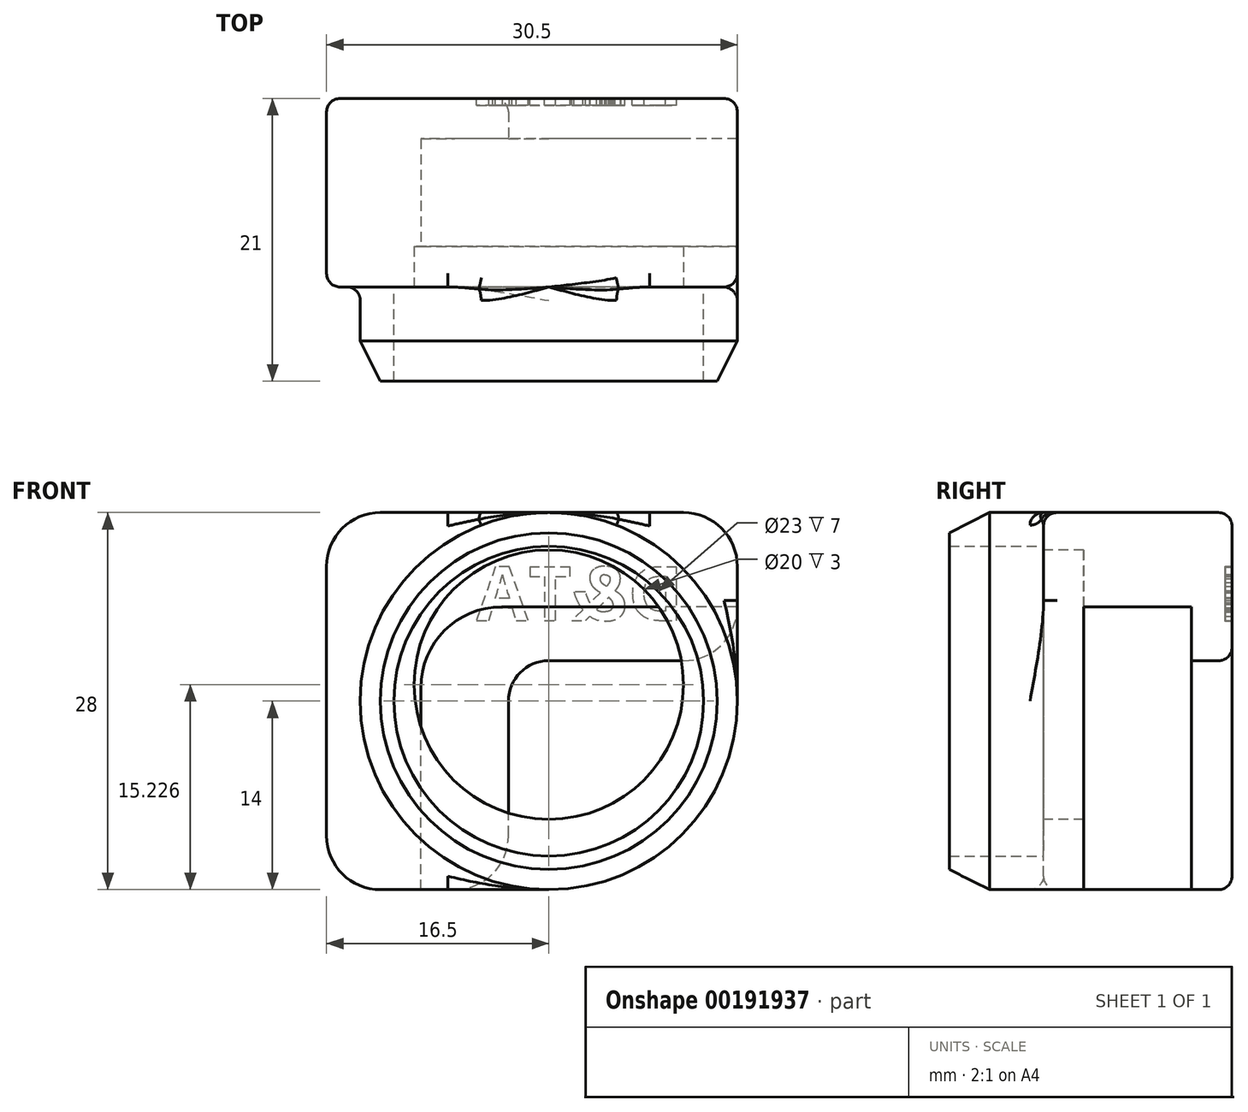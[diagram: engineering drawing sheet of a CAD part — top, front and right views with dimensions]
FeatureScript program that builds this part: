
annotation { "Feature Type Name" : "Feature", "Feature Type Description" : "" }
export const myFeature = defineFeature(function(context is Context, id is Id, definition is map)
    precondition{}
    {
        {
            var Q0;
            Q0=qCreatedBy(makeId("Front.planeOp"),FACE);
            var sketch = newSketch(context, id + "F0", { "sketchPlane" : qUnion([Q0])});
            skCircle(sketch, "E0", {"center": v(0, 0) * mm, "radius": 14 * mm});
            skCircle(sketch, "E1", {"center": v(0, 0) * mm, "radius": 11.5 * mm});
            skSolve(sketch);
        }
        {
            var Q0;
            Q0=makeQuery(id+"F0.imprint","IMPRINT",FACE,{"disambiguationData":[TD([[makeQuery(id+"F0.imprint","IMPRINT",EDGE,{"derivedFrom":sQuery(id+"F0.wireOp",EDGE,"E0")}),1.0]])]});
            extrude(context, id + "F1", {"entities" : qUnion([Q0]), "depth" : 10 * mm});
        }
        {
            var Q0;
            Q0=qCreatedBy(makeId("Front.planeOp"),FACE);
            var sketch = newSketch(context, id + "F2", { "sketchPlane" : qUnion([Q0])});
            skLineSegment(sketch, "E2", {"start": v(-9.5, -14) * mm, "end": v(-16.5, -14) * mm});
            skLineSegment(sketch, "E3", {"start": v(-16.5, -14) * mm, "end": v(-16.5, 14) * mm});
            skLineSegment(sketch, "E4", {"start": v(-16.5, 14) * mm, "end": v(14, 14) * mm});
            skLineSegment(sketch, "E5", {"start": v(14, 14) * mm, "end": v(14, 7) * mm});
            skLineSegment(sketch, "E6", {"start": v(14, 7) * mm, "end": v(-3.5, 7) * mm});
            skLineSegment(sketch, "E7", {"start": v(-9.5, -14) * mm, "end": v(-9.5, 1) * mm});
            skArc(sketch, "E8", {"start": v(-3.5, 7) * mm, "mid": v(-7.74, 5.24) * mm, "end": v(-9.5, 1) * mm});
            skSolve(sketch);
        }
        {
            var Q0;
            Q0=makeQuery(id+"F2.imprint","IMPRINT",FACE,{"disambiguationData":[TD([[makeQuery(id+"F2.imprint","IMPRINT",EDGE,{"derivedFrom":sQuery(id+"F2.wireOp",EDGE,"E2")}),-1.0]])]});
            extrude(context, id + "F3", {"entities" : qUnion([Q0]), "operationType" : NewBodyOperationType.ADD, "oppositeDirection" : true, "depth" : 8 * mm});
        }
        {
            var Q0;
            Q0=makeQuery(id+"F1.opExtrude","CAP_FACE",FACE,{"disambiguationData":[OSD([sQuery(id+"F0.wireOp",EDGE,"E0"),sQuery(id+"F0.wireOp",EDGE,"E1")])],"isStart":true});
            var sketch = newSketch(context, id + "F4", { "sketchPlane" : qUnion([Q0])});
            skArc(sketch, "E9", {"start": v(-14, 0) * mm, "mid": v(-9.9, -9.9) * mm, "end": v(0, -14) * mm});
            skLineSegment(sketch, "E10", {"start": v(16.5, 14) * mm, "end": v(-14, 14) * mm});
            skLineSegment(sketch, "E11", {"start": v(-14, 14) * mm, "end": v(-14, 0) * mm});
            skLineSegment(sketch, "E12", {"start": v(16.5, 14) * mm, "end": v(16.5, -14) * mm});
            skLineSegment(sketch, "E13", {"start": v(16.5, -14) * mm, "end": v(0, -14) * mm});
            skSolve(sketch);
        }
        {
            var Q0;
            Q0=makeQuery(id+"F4.imprint","IMPRINT",FACE,{"disambiguationData":[TD([[makeQuery(id+"F4.imprint","IMPRINT",EDGE,{"derivedFrom":sQuery(id+"F4.wireOp",EDGE,"E10")}),1.0]])]});
            extrude(context, id + "F5", {"entities" : qUnion([Q0]), "operationType" : NewBodyOperationType.ADD, "oppositeDirection" : true, "depth" : 3 * mm});
        }
        {
            var Q0;
            Q0=makeQuery(id+"F3.opExtrude","CAP_FACE",FACE,{"disambiguationData":[OSD([sQuery(id+"F2.wireOp",EDGE,"E2"),sQuery(id+"F2.wireOp",EDGE,"E3"),sQuery(id+"F2.wireOp",EDGE,"E4"),sQuery(id+"F2.wireOp",EDGE,"E5"),sQuery(id+"F2.wireOp",EDGE,"E6"),sQuery(id+"F2.wireOp",EDGE,"E7"),sQuery(id+"F2.wireOp",EDGE,"E8")])],"isStart":false});
            var sketch = newSketch(context, id + "F6", { "sketchPlane" : qUnion([Q0])});
            skLineSegment(sketch, "E14", {"start": v(-14, 14) * mm, "end": v(16.5, 14) * mm});
            skLineSegment(sketch, "E15", {"start": v(16.5, 14) * mm, "end": v(16.5, -14) * mm});
            skLineSegment(sketch, "E16", {"start": v(16.5, -14) * mm, "end": v(3, -14) * mm});
            skLineSegment(sketch, "E17", {"start": v(3, -14) * mm, "end": v(3, 0) * mm});
            skLineSegment(sketch, "E18", {"start": v(-14, 14) * mm, "end": v(-14, 3) * mm});
            skLineSegment(sketch, "E19", {"start": v(-14, 3) * mm, "end": v(0, 3) * mm});
            skArc(sketch, "E20", {"start": v(3, 0) * mm, "mid": v(2.12, 2.12) * mm, "end": v(0, 3) * mm});
            skSolve(sketch);
        }
        {
            var Q0;
            {var subQ0=sQuery(id+"F0.wireOp",EDGE,"E0");Q0=makeQuery(id+"F5.boolean.opBoolean","INTERSECT",EDGE,{"disambiguationData":[OD(0.0)],"derivedFrom":[makeQuery(id+"F1.opExtrude","SWEPT_FACE",FACE,{"disambiguationData":[OSD([subQ0])]}),makeQuery(id+"F5.opExtrude","CAP_FACE",FACE,{"disambiguationData":[OSD([subQ0,sQuery(id+"F0.wireOp",EDGE,"E1"),sQuery(id+"F2.wireOp",EDGE,"E6"),sQuery(id+"F2.wireOp",EDGE,"E7"),sQuery(id+"F4.wireOp",EDGE,"E10"),sQuery(id+"F4.wireOp",EDGE,"E11"),sQuery(id+"F4.wireOp",EDGE,"E12"),sQuery(id+"F4.wireOp",EDGE,"E13")])],"isStart":false})]});}
            fillet(context, id + "F7", {"entities" : qUnion([Q0]), "radius" : 1 * mm, "tangentPropagation" : true, "allowEdgeOverflow" : false});
        }
        {
            var Q0;
            {var subQ3=sQuery(id+"F6.wireOp",EDGE,"E17");Q0=makeQuery(id+"F6.imprint","IMPRINT",FACE,{"disambiguationData":[TD([[makeQuery(id+"F6.imprint","IMPRINT",EDGE,{"derivedFrom":subQ3}),-1.0]])]});}
            var Q1;
            {var subQ4=sQuery(id+"F6.wireOp",EDGE,"E14");Q1=makeQuery(id+"F6.imprint","IMPRINT",FACE,{"disambiguationData":[TD([[makeQuery(id+"F6.imprint","IMPRINT",EDGE,{"derivedFrom":subQ4}),1.0]])]});}
            extrude(context, id + "F8", {"entities" : qUnion([Q0, Q1]), "operationType" : NewBodyOperationType.ADD, "depth" : 3 * mm});
        }
        {
            var Q0;
            Q0=makeQuery(id+"F8.boolean.opBoolean","MERGE",EDGE,{"derivedFrom":[makeQuery(id+"F5.boolean.opBoolean","MERGE",EDGE,{"derivedFrom":[makeQuery(id+"F3.opExtrude","SWEPT_EDGE",EDGE,{"disambiguationData":[OSD([sQuery(id+"F2.wireOp",EDGE,"E2"),sQuery(id+"F2.wireOp",EDGE,"E3")])]}),makeQuery(id+"F5.opExtrude","SWEPT_EDGE",EDGE,{"disambiguationData":[OSD([sQuery(id+"F4.wireOp",EDGE,"E12"),sQuery(id+"F4.wireOp",EDGE,"E13")])]})]}),makeQuery(id+"F8.opExtrude","SWEPT_EDGE",EDGE,{"disambiguationData":[OSD([sQuery(id+"F6.wireOp",EDGE,"E15"),sQuery(id+"F6.wireOp",EDGE,"E16")])]})]});
            var Q1;
            Q1=makeQuery(id+"F8.boolean.opBoolean","MERGE",EDGE,{"derivedFrom":[makeQuery(id+"F5.boolean.opBoolean","MERGE",EDGE,{"derivedFrom":[makeQuery(id+"F3.opExtrude","SWEPT_EDGE",EDGE,{"disambiguationData":[OSD([sQuery(id+"F2.wireOp",EDGE,"E4"),sQuery(id+"F2.wireOp",EDGE,"E5")])]}),makeQuery(id+"F5.opExtrude","SWEPT_EDGE",EDGE,{"disambiguationData":[OSD([sQuery(id+"F4.wireOp",EDGE,"E10"),sQuery(id+"F4.wireOp",EDGE,"E11")])]})]}),makeQuery(id+"F8.opExtrude","SWEPT_EDGE",EDGE,{"disambiguationData":[OSD([sQuery(id+"F6.wireOp",EDGE,"E14"),sQuery(id+"F6.wireOp",EDGE,"E18")])]})]});
            var Q2;
            Q2=makeQuery(id+"F8.opExtrude","SWEPT_EDGE",EDGE,{"disambiguationData":[OSD([sQuery(id+"F6.wireOp",EDGE,"E16"),sQuery(id+"F6.wireOp",EDGE,"E17")])]});
            var Q3;
            Q3=makeQuery(id+"F8.opExtrude","SWEPT_EDGE",EDGE,{"disambiguationData":[OSD([sQuery(id+"F6.wireOp",EDGE,"E18"),sQuery(id+"F6.wireOp",EDGE,"E19")])]});
            var Q4;
            Q4=makeQuery(id+"F8.boolean.opBoolean","MERGE",EDGE,{"derivedFrom":[makeQuery(id+"F5.boolean.opBoolean","MERGE",EDGE,{"derivedFrom":[makeQuery(id+"F3.opExtrude","SWEPT_EDGE",EDGE,{"disambiguationData":[OSD([sQuery(id+"F2.wireOp",EDGE,"E3"),sQuery(id+"F2.wireOp",EDGE,"E4")])]}),makeQuery(id+"F5.opExtrude","SWEPT_EDGE",EDGE,{"disambiguationData":[OSD([sQuery(id+"F4.wireOp",EDGE,"E10"),sQuery(id+"F4.wireOp",EDGE,"E12")])]})]}),makeQuery(id+"F8.opExtrude","SWEPT_EDGE",EDGE,{"disambiguationData":[OSD([sQuery(id+"F6.wireOp",EDGE,"E14"),sQuery(id+"F6.wireOp",EDGE,"E15")])]})]});
            fillet(context, id + "F9", {"entities" : qUnion([Q0, Q1, Q2, Q3, Q4]), "radius" : 4 * mm, "tangentPropagation" : true, "allowEdgeOverflow" : false});
        }
        {
            var Q0;
            {var subQ0=sQuery(id+"F2.wireOp",EDGE,"E4");var subQ1=sQuery(id+"F2.wireOp",EDGE,"E3");var subQ2=sQuery(id+"F4.wireOp",EDGE,"E12");var subQ3=sQuery(id+"F0.wireOp",EDGE,"E0");var subQ4=sQuery(id+"F4.wireOp",EDGE,"E10");var subQ5=sQuery(id+"F4.wireOp",EDGE,"E13");var subQ6=makeQuery(id+"F5.opExtrude","CAP_FACE",FACE,{"disambiguationData":[OSD([subQ3,sQuery(id+"F0.wireOp",EDGE,"E1"),sQuery(id+"F2.wireOp",EDGE,"E6"),sQuery(id+"F2.wireOp",EDGE,"E7"),subQ4,sQuery(id+"F4.wireOp",EDGE,"E11"),subQ2,subQ5])],"isStart":false});Q0=makeQuery(id+"F9.opFillet","BLEND_EDGE",EDGE,{"blendedFrom":[makeQuery(id+"F8.boolean.opBoolean","MERGE",EDGE,{"derivedFrom":[makeQuery(id+"F5.boolean.opBoolean","MERGE",EDGE,{"derivedFrom":[makeQuery(id+"F3.opExtrude","SWEPT_EDGE",EDGE,{"disambiguationData":[OSD([subQ1,subQ0])]}),makeQuery(id+"F5.opExtrude","SWEPT_EDGE",EDGE,{"disambiguationData":[OSD([subQ4,subQ2])]})]}),makeQuery(id+"F8.opExtrude","SWEPT_EDGE",EDGE,{"disambiguationData":[OSD([sQuery(id+"F6.wireOp",EDGE,"E14"),sQuery(id+"F6.wireOp",EDGE,"E15")])]})]}),makeQuery(id+"F5.boolean.opBoolean","SPLIT",FACE,{"disambiguationData":[TD([makeQuery(id+"F3.opExtrude","SWEPT_FACE",FACE,{"disambiguationData":[OSD([sQuery(id+"F2.wireOp",EDGE,"E2")])]})])],"derivedFrom":subQ6})],"blendedInto":[makeQuery(id+"F5.boolean.opBoolean","SPLIT",FACE,{"disambiguationData":[TD([makeQuery(id+"F3.opExtrude","SWEPT_FACE",FACE,{"disambiguationData":[OSD([sQuery(id+"F2.wireOp",EDGE,"E2")])]})])],"derivedFrom":subQ6})]});}
            var Q1;
            Q1=makeQuery(id+"F8.opExtrude","CAP_EDGE",EDGE,{"disambiguationData":[OSD([sQuery(id+"F6.wireOp",EDGE,"E14")])],"isStart":false});
            var Q2;
            {var subQ0=sQuery(id+"F4.wireOp",EDGE,"E10");var subQ1=sQuery(id+"F2.wireOp",EDGE,"E5");var subQ2=sQuery(id+"F2.wireOp",EDGE,"E4");var subQ3=sQuery(id+"F0.wireOp",EDGE,"E0");var subQ4=sQuery(id+"F4.wireOp",EDGE,"E11");var subQ5=makeQuery(id+"F5.opExtrude","CAP_FACE",FACE,{"disambiguationData":[OSD([subQ3,sQuery(id+"F0.wireOp",EDGE,"E1"),sQuery(id+"F2.wireOp",EDGE,"E6"),sQuery(id+"F2.wireOp",EDGE,"E7"),subQ0,subQ4,sQuery(id+"F4.wireOp",EDGE,"E12"),sQuery(id+"F4.wireOp",EDGE,"E13")])],"isStart":false});Q2=makeQuery(id+"F9.opFillet","BLEND_EDGE",EDGE,{"blendedFrom":[makeQuery(id+"F8.boolean.opBoolean","MERGE",EDGE,{"derivedFrom":[makeQuery(id+"F5.boolean.opBoolean","MERGE",EDGE,{"derivedFrom":[makeQuery(id+"F3.opExtrude","SWEPT_EDGE",EDGE,{"disambiguationData":[OSD([subQ2,subQ1])]}),makeQuery(id+"F5.opExtrude","SWEPT_EDGE",EDGE,{"disambiguationData":[OSD([subQ0,subQ4])]})]}),makeQuery(id+"F8.opExtrude","SWEPT_EDGE",EDGE,{"disambiguationData":[OSD([sQuery(id+"F6.wireOp",EDGE,"E14"),sQuery(id+"F6.wireOp",EDGE,"E18")])]})]}),makeQuery(id+"F5.boolean.opBoolean","SPLIT",FACE,{"disambiguationData":[TD([makeQuery(id+"F3.opExtrude","SWEPT_FACE",FACE,{"disambiguationData":[OSD([subQ1])]})])],"derivedFrom":subQ5})],"blendedInto":[makeQuery(id+"F5.boolean.opBoolean","SPLIT",FACE,{"disambiguationData":[TD([makeQuery(id+"F3.opExtrude","SWEPT_FACE",FACE,{"disambiguationData":[OSD([subQ1])]})])],"derivedFrom":subQ5})]});}
            fillet(context, id + "F10", {"entities" : qUnion([Q0, Q1, Q2]), "radius" : 1 * mm, "tangentPropagation" : true, "allowEdgeOverflow" : false});
        }
        {
            var Q0;
            {var subQ0=sQuery(id+"F0.wireOp",EDGE,"E1");Q0=makeQuery(id+"F5.boolean.opBoolean","SPLIT",FACE,{"disambiguationData":[TD([makeQuery(id+"F1.opExtrude","SWEPT_FACE",FACE,{"disambiguationData":[OSD([subQ0])]})])],"derivedFrom":makeQuery(id+"F5.opExtrude","CAP_FACE",FACE,{"disambiguationData":[OSD([sQuery(id+"F0.wireOp",EDGE,"E0"),subQ0,sQuery(id+"F2.wireOp",EDGE,"E6"),sQuery(id+"F2.wireOp",EDGE,"E7"),sQuery(id+"F4.wireOp",EDGE,"E10"),sQuery(id+"F4.wireOp",EDGE,"E11"),sQuery(id+"F4.wireOp",EDGE,"E12"),sQuery(id+"F4.wireOp",EDGE,"E13")])],"isStart":false})});}
            var sketch = newSketch(context, id + "F11", { "sketchPlane" : qUnion([Q0])});
            skCircle(sketch, "E21", {"center": v(0, 1.23) * mm, "radius": 10 * mm});
            skSolve(sketch);
        }
        {
            var Q0;
            Q0=makeQuery(id+"F11.imprint","IMPRINT",FACE,{"disambiguationData":[TD([[makeQuery(id+"F11.imprint","IMPRINT",EDGE,{"derivedFrom":sQuery(id+"F11.wireOp",EDGE,"E21")}),1.0]])]});
            var Q1;
            {var subQ0=sQuery(id+"F0.wireOp",EDGE,"E1");var subQ1=sQuery(id+"F0.wireOp",EDGE,"E0");Q1=makeQuery(id+"F5.boolean.opBoolean","MERGE",FACE,{"derivedFrom":[makeQuery(id+"F1.opExtrude","CAP_FACE",FACE,{"disambiguationData":[OSD([subQ1,subQ0])],"isStart":true}),makeQuery(id+"F5.opExtrude","CAP_FACE",FACE,{"disambiguationData":[OSD([subQ1,subQ0,sQuery(id+"F2.wireOp",EDGE,"E6"),sQuery(id+"F2.wireOp",EDGE,"E7"),sQuery(id+"F4.wireOp",EDGE,"E10"),sQuery(id+"F4.wireOp",EDGE,"E11"),sQuery(id+"F4.wireOp",EDGE,"E12"),sQuery(id+"F4.wireOp",EDGE,"E13")])],"isStart":true})]});}
            extrude(context, id + "F12", {"entities" : qUnion([Q0]), "operationType" : NewBodyOperationType.REMOVE, "endBound" : BoundingType.UP_TO_SURFACE, "oppositeDirection" : true, "endBoundEntityFace" : qUnion([Q1]), "depth" : 25 * mm});
        }
        {
            var Q0;
            Q0=makeQuery(id+"F8.opExtrude","CAP_FACE",FACE,{"disambiguationData":[OSD([sQuery(id+"F6.wireOp",EDGE,"E14"),sQuery(id+"F6.wireOp",EDGE,"E15"),sQuery(id+"F6.wireOp",EDGE,"E16"),sQuery(id+"F6.wireOp",EDGE,"E17"),sQuery(id+"F6.wireOp",EDGE,"E18"),sQuery(id+"F6.wireOp",EDGE,"E19"),sQuery(id+"F6.wireOp",EDGE,"E20")])],"isStart":false});
            var sketch = newSketch(context, id + "F13", { "sketchPlane" : qUnion([Q0])});
            skText(sketch, "E22", { "text": "D&TA", "fontName": "OpenSans-Bold.ttf"});
            const initialGuessF13  = {"E22": [-0.01, 0.00599, 1, 0, 0.00401]};
            skSetInitialGuess(sketch, initialGuessF13);
            skSolve(sketch);
        }
        {
            var Q0;
            Q0 = qSketchRegion(id + "F13", true);
            extrude(context, id + "F14", {"entities" : qUnion([Q0]), "operationType" : NewBodyOperationType.REMOVE, "oppositeDirection" : true, "depth" : 0.5 * mm});
        }
        {
            var Q0;
            Q0=makeQuery(id+"F1.opExtrude","CAP_EDGE",EDGE,{"disambiguationData":[OSD([sQuery(id+"F0.wireOp",EDGE,"E0")])],"isStart":false});
            chamfer(context, id + "F15", {"entities" : qUnion([Q0]), "chamferType" : ChamferType.TWO_OFFSETS, "width1" : 1.5 * mm, "oppositeDirection" : false, "width2" : 3 * mm, "tangentPropagation" : true});
        }
    });
